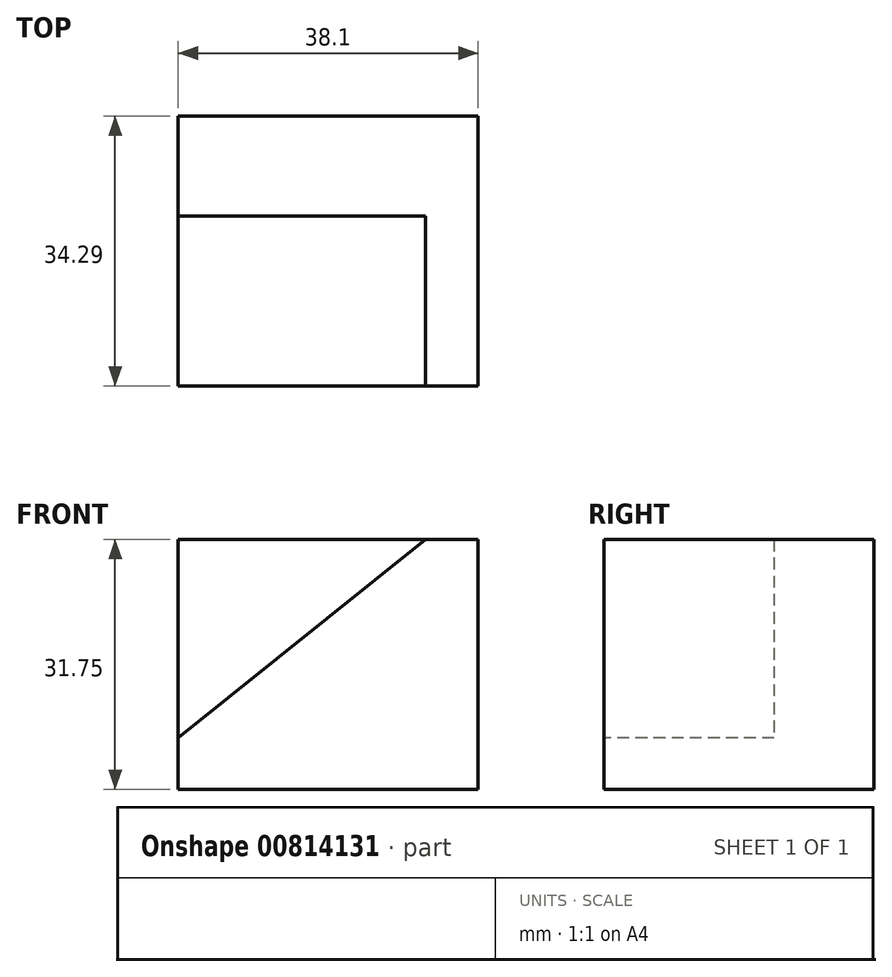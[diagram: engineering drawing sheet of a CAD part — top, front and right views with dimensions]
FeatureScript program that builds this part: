
annotation { "Feature Type Name" : "Feature", "Feature Type Description" : "" }
export const myFeature = defineFeature(function(context is Context, id is Id, definition is map)
    precondition{}
    {
        {
            var Q0;
            Q0=qCreatedBy(makeId("Top.planeOp"),FACE);
            var sketch = newSketch(context, id + "F0", { "sketchPlane" : qUnion([Q0])});
            skLineSegment(sketch, "E0.bottom", {"start": v(0, 0) * mm, "end": v(38.1, 0) * mm});
            skLineSegment(sketch, "E0.top", {"start": v(0, 25.4) * mm, "end": v(38.1, 25.4) * mm});
            skLineSegment(sketch, "E0.left", {"start": v(0, 0) * mm, "end": v(0, 25.4) * mm});
            skLineSegment(sketch, "E0.right", {"start": v(38.1, 0) * mm, "end": v(38.1, 25.4) * mm});
            skSolve(sketch);
        }
        {
            var Q0;
            Q0=qCreatedBy(makeId("Front.planeOp"),FACE);
            var sketch = newSketch(context, id + "F1", { "sketchPlane" : qUnion([Q0])});
            skSolve(sketch);
        }
        {
            var Q0;
            Q0=qSketchRegion(id+"F1",true);
            var Q1;
            Q1=qSketchRegion(id+"F0",true);
            extrude(context, id + "F2", {"entities" : qUnion([Q0, Q1]), "depth" : 31.75 * mm, "offsetDistance" : 25.4 * mm});
        }
        {
            var Q0;
            Q0=makeQuery(id+"F2.opExtrude","SWEPT_FACE",FACE,{"disambiguationData":[OSD([sQuery(id+"F0.wireOp",EDGE,"E0.bottom")])]});
            var sketch = newSketch(context, id + "F3", { "sketchPlane" : qUnion([Q0])});
            skLineSegment(sketch, "E1", {"start": v(0, 0) * mm, "end": v(0, 6.52) * mm});
            skLineSegment(sketch, "E2", {"start": v(38.1, 31.75) * mm, "end": v(31.44, 31.75) * mm});
            skLineSegment(sketch, "E3", {"start": v(0, 6.52) * mm, "end": v(31.44, 31.75) * mm});
            skSolve(sketch);
        }
        {
            var Q0;
            {var subQ0=sQuery(id+"F3.wireOp",EDGE,"E3");Q0=makeQuery(id+"F3.imprint","IMPRINT",FACE,{"disambiguationData":[TD([[makeQuery(id+"F3.imprint","IMPRINT",EDGE,{"derivedFrom":subQ0}),1.0]])]});}
            extrude(context, id + "F4", {"entities" : qUnion([Q0]), "operationType" : NewBodyOperationType.REMOVE, "oppositeDirection" : true, "depth" : 12.7 * mm, "offsetDistance" : 25.4 * mm});
        }
        {
            var Q0;
            Q0=makeQuery(id+"F2.opExtrude","SWEPT_FACE",FACE,{"disambiguationData":[OSD([sQuery(id+"F0.wireOp",EDGE,"E0.bottom")])]});
            extrude(context, id + "F5", {"entities" : qUnion([Q0]), "operationType" : NewBodyOperationType.ADD, "depth" : 8.9 * mm, "offsetDistance" : 25.4 * mm});
        }
    });
